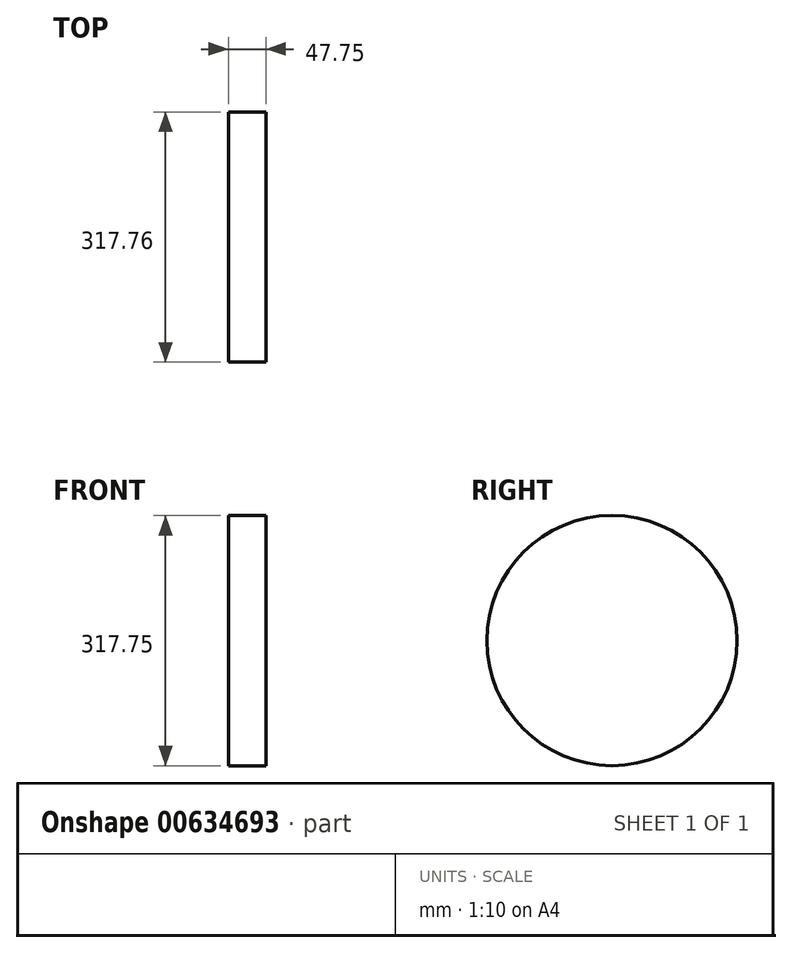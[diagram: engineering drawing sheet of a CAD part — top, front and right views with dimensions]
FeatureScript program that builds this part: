
annotation { "Feature Type Name" : "Feature", "Feature Type Description" : "" }
export const myFeature = defineFeature(function(context is Context, id is Id, definition is map)
    precondition{}
    {
        {
            var Q0;
            Q0=qCreatedBy(makeId("Right.planeOp"),FACE);
            var sketch = newSketch(context, id + "F0", { "sketchPlane" : qUnion([Q0])});
            skCircle(sketch, "E0", {"center": v(68.98, 39.03) * mm, "radius": 158.88 * mm});
            skSolve(sketch);
        }
        {
            var Q0;
            Q0=makeQuery(id+"F0.imprint","IMPRINT",FACE,{"disambiguationData":[TD([[makeQuery(id+"F0.imprint","IMPRINT",EDGE,{"derivedFrom":sQuery(id+"F0.wireOp",EDGE,"E0")}),1.0]])]});
            extrude(context, id + "F1", {"entities" : qUnion([Q0]), "depth" : 47.75 * mm, "offsetDistance" : 25.4 * mm});
        }
    });
